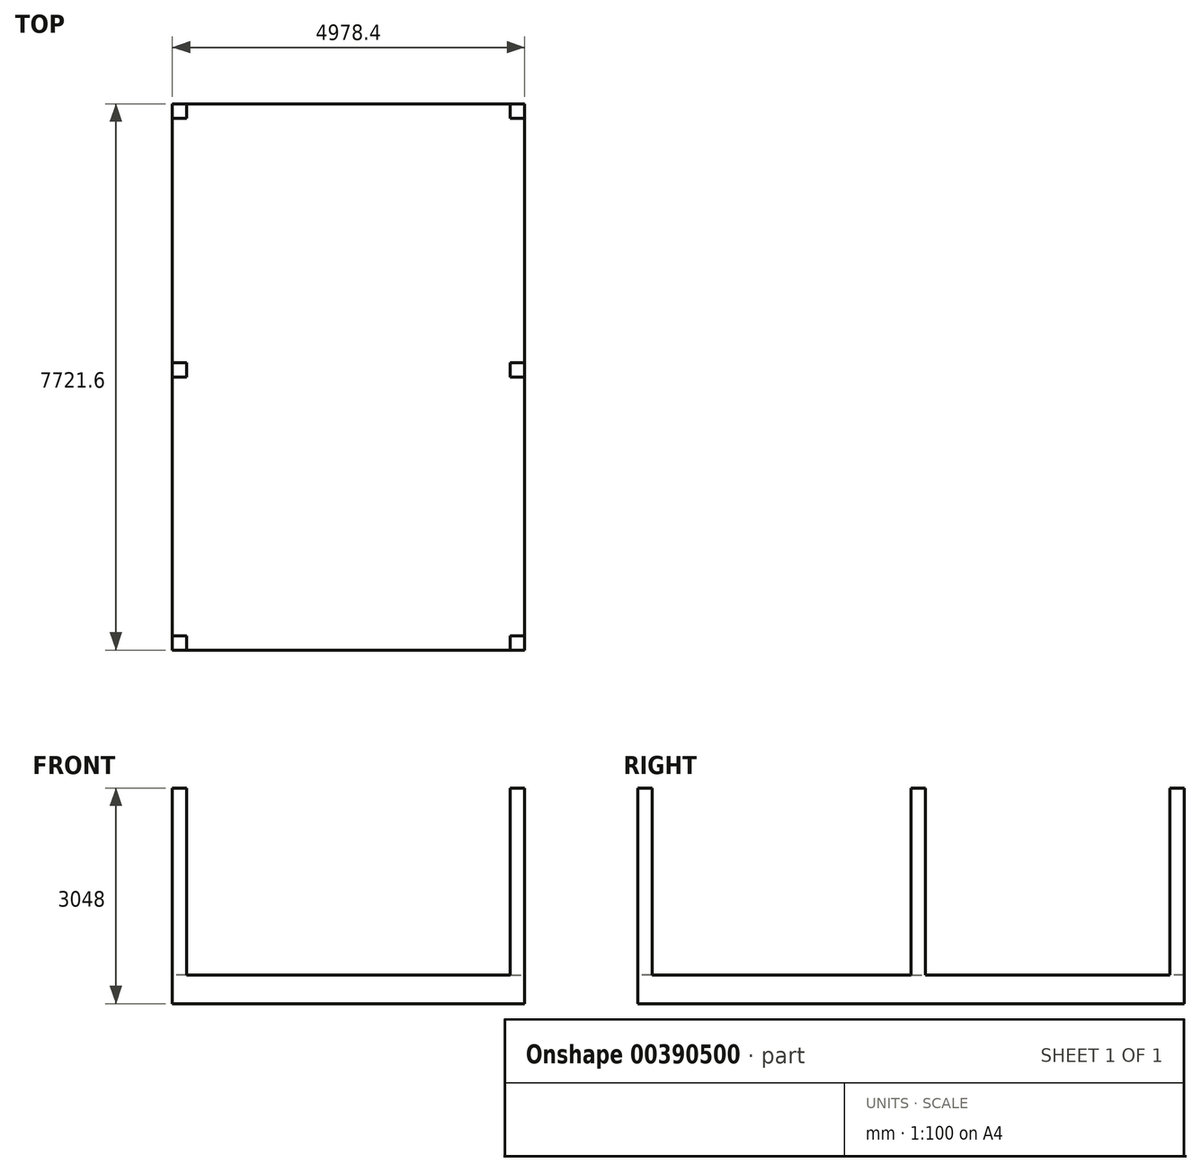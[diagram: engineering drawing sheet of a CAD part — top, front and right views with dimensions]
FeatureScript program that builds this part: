
annotation { "Feature Type Name" : "Feature", "Feature Type Description" : "" }
export const myFeature = defineFeature(function(context is Context, id is Id, definition is map)
    precondition{}
    {
        {
            var Q0;
            Q0=qCreatedBy(makeId("Top.planeOp"),FACE);
            var sketch = newSketch(context, id + "F0", { "sketchPlane" : qUnion([Q0])});
            skLineSegment(sketch, "E0.bottom", {"start": v(-2489.53, 5036.96) * mm, "end": v(2488.87, 5036.96) * mm});
            skLineSegment(sketch, "E0.top", {"start": v(-2489.53, -2684.64) * mm, "end": v(2488.87, -2684.64) * mm});
            skLineSegment(sketch, "E0.left", {"start": v(-2489.53, 5036.96) * mm, "end": v(-2489.53, -2684.64) * mm});
            skLineSegment(sketch, "E0.right", {"start": v(2488.87, 5036.96) * mm, "end": v(2488.87, -2684.64) * mm});
            skSolve(sketch);
        }
        {
            var Q0;
            Q0 = qSketchRegion(id + "F0", true);
            extrude(context, id + "F1", {"entities" : qUnion([Q0]), "oppositeDirection" : true, "depth" : 406.4 * mm});
        }
        {
            var Q0;
            Q0=makeQuery(id+"F1.opExtrude","SWEPT_FACE",FACE,{"disambiguationData":[OSD([sQuery(id+"F0.wireOp",EDGE,"E0.right")])]});
            var sketch = newSketch(context, id + "F2", { "sketchPlane" : qUnion([Q0])});
            skSolve(sketch);
        }
        {
            var Q0;
            Q0=makeQuery(id+"F1.opExtrude","CAP_FACE",FACE,{"disambiguationData":[OSD([sQuery(id+"F0.wireOp",EDGE,"E0.bottom"),sQuery(id+"F0.wireOp",EDGE,"E0.top"),sQuery(id+"F0.wireOp",EDGE,"E0.left"),sQuery(id+"F0.wireOp",EDGE,"E0.right")])],"isStart":false});
            var sketch = newSketch(context, id + "F3", { "sketchPlane" : qUnion([Q0])});
            skLineSegment(sketch, "E1.bottom", {"start": v(-2489.53, 2684.64) * mm, "end": v(-2286.33, 2684.64) * mm});
            skLineSegment(sketch, "E1.top", {"start": v(-2489.53, 2481.44) * mm, "end": v(-2286.33, 2481.44) * mm});
            skLineSegment(sketch, "E1.left", {"start": v(-2489.53, 2684.64) * mm, "end": v(-2489.53, 2481.44) * mm});
            skLineSegment(sketch, "E1.right", {"start": v(-2286.33, 2684.64) * mm, "end": v(-2286.33, 2481.44) * mm});
            skSolve(sketch);
        }
        {
            var Q0;
            Q0=makeQuery(id+"F3.imprint","IMPRINT",FACE,{"disambiguationData":[TD([[makeQuery(id+"F3.imprint","IMPRINT",EDGE,{"derivedFrom":sQuery(id+"F3.wireOp",EDGE,"E1.bottom")}),-1.0]])]});
            extrude(context, id + "F4", {"entities" : qUnion([Q0]), "operationType" : NewBodyOperationType.ADD, "oppositeDirection" : true, "depth" : 3048 * mm});
        }
        {
            var Q0;
            Q0=makeQuery(id+"F1.opExtrude","CAP_FACE",FACE,{"disambiguationData":[OSD([sQuery(id+"F0.wireOp",EDGE,"E0.bottom"),sQuery(id+"F0.wireOp",EDGE,"E0.top"),sQuery(id+"F0.wireOp",EDGE,"E0.left"),sQuery(id+"F0.wireOp",EDGE,"E0.right")])],"isStart":false});
            var sketch = newSketch(context, id + "F5", { "sketchPlane" : qUnion([Q0])});
            skLineSegment(sketch, "E2.bottom", {"start": v(2488.87, 2684.64) * mm, "end": v(2285.67, 2684.64) * mm});
            skLineSegment(sketch, "E2.top", {"start": v(2488.87, 2481.44) * mm, "end": v(2285.67, 2481.44) * mm});
            skLineSegment(sketch, "E2.left", {"start": v(2488.87, 2684.64) * mm, "end": v(2488.87, 2481.44) * mm});
            skLineSegment(sketch, "E2.right", {"start": v(2285.67, 2684.64) * mm, "end": v(2285.67, 2481.44) * mm});
            skSolve(sketch);
        }
        {
            var Q0;
            Q0=makeQuery(id+"F5.imprint","IMPRINT",FACE,{"disambiguationData":[TD([[makeQuery(id+"F5.imprint","IMPRINT",EDGE,{"derivedFrom":sQuery(id+"F5.wireOp",EDGE,"E2.bottom")}),-1.0]])]});
            extrude(context, id + "F6", {"entities" : qUnion([Q0]), "operationType" : NewBodyOperationType.ADD, "oppositeDirection" : true, "depth" : 3048 * mm});
        }
        {
            var Q0;
            Q0=makeQuery(id+"F0.imprint","IMPRINT",FACE,{"disambiguationData":[TD([[makeQuery(id+"F0.imprint","IMPRINT",EDGE,{"derivedFrom":sQuery(id+"F0.wireOp",EDGE,"E0.bottom")}),-1.0]])]});
            var sketch = newSketch(context, id + "F7", { "sketchPlane" : qUnion([Q0])});
            skSolve(sketch);
        }
        {
            var Q0;
            {var subQ2=sQuery(id+"F5.wireOp",EDGE,"E2.top");Q0=makeQuery(id+"F5.imprint","IMPRINT",FACE,{"disambiguationData":[TD([[makeQuery(id+"F5.imprint","IMPRINT",EDGE,{"derivedFrom":subQ2}),1.0]])]});}
            var sketch = newSketch(context, id + "F8", { "sketchPlane" : qUnion([Q0])});
            skLineSegment(sketch, "E3.bottom", {"start": v(2285.67, -4833.76) * mm, "end": v(2488.87, -4833.76) * mm});
            skLineSegment(sketch, "E3.top", {"start": v(2285.67, -5036.96) * mm, "end": v(2488.87, -5036.96) * mm});
            skLineSegment(sketch, "E3.left", {"start": v(2285.67, -4833.76) * mm, "end": v(2285.67, -5036.96) * mm});
            skLineSegment(sketch, "E3.right", {"start": v(2488.87, -4833.76) * mm, "end": v(2488.87, -5036.96) * mm});
            skSolve(sketch);
        }
        {
            var Q0;
            Q0 = qSketchRegion(id + "F8", true);
            extrude(context, id + "F9", {"entities" : qUnion([Q0]), "operationType" : NewBodyOperationType.ADD, "oppositeDirection" : true, "depth" : 3048 * mm});
        }
        {
            var Q0;
            {var subQ2=sQuery(id+"F5.wireOp",EDGE,"E2.top");Q0=makeQuery(id+"F5.imprint","IMPRINT",FACE,{"disambiguationData":[TD([[makeQuery(id+"F5.imprint","IMPRINT",EDGE,{"derivedFrom":subQ2}),1.0]])]});}
            var sketch = newSketch(context, id + "F10", { "sketchPlane" : qUnion([Q0])});
            skLineSegment(sketch, "E4.bottom", {"start": v(-2489.53, -4833.76) * mm, "end": v(-2286.33, -4833.76) * mm});
            skLineSegment(sketch, "E4.top", {"start": v(-2489.53, -5036.96) * mm, "end": v(-2286.33, -5036.96) * mm});
            skLineSegment(sketch, "E4.left", {"start": v(-2489.53, -4833.76) * mm, "end": v(-2489.53, -5036.96) * mm});
            skLineSegment(sketch, "E4.right", {"start": v(-2286.33, -4833.76) * mm, "end": v(-2286.33, -5036.96) * mm});
            skSolve(sketch);
        }
        {
            var Q0;
            Q0 = qSketchRegion(id + "F10", true);
            extrude(context, id + "F11", {"entities" : qUnion([Q0]), "operationType" : NewBodyOperationType.ADD, "oppositeDirection" : true, "depth" : 3048 * mm});
        }
        {
            var Q0;
            {var subQ2=sQuery(id+"F5.wireOp",EDGE,"E2.top");Q0=makeQuery(id+"F5.imprint","IMPRINT",FACE,{"disambiguationData":[TD([[makeQuery(id+"F5.imprint","IMPRINT",EDGE,{"derivedFrom":subQ2}),1.0]])]});}
            var sketch = newSketch(context, id + "F12", { "sketchPlane" : qUnion([Q0])});
            skLineSegment(sketch, "E5.bottom", {"start": v(-2286.33, -1379.36) * mm, "end": v(-2489.53, -1379.36) * mm});
            skLineSegment(sketch, "E5.top", {"start": v(-2286.33, -1176.16) * mm, "end": v(-2489.53, -1176.16) * mm});
            skLineSegment(sketch, "E5.left", {"start": v(-2286.33, -1379.36) * mm, "end": v(-2286.33, -1176.16) * mm});
            skLineSegment(sketch, "E5.right", {"start": v(-2489.53, -1379.36) * mm, "end": v(-2489.53, -1176.16) * mm});
            skSolve(sketch);
        }
        {
            var Q0;
            Q0 = qSketchRegion(id + "F12", true);
            extrude(context, id + "F13", {"entities" : qUnion([Q0]), "operationType" : NewBodyOperationType.ADD, "oppositeDirection" : true, "depth" : 3048 * mm});
        }
        {
            var Q0;
            {var subQ2=sQuery(id+"F5.wireOp",EDGE,"E2.top");Q0=makeQuery(id+"F5.imprint","IMPRINT",FACE,{"disambiguationData":[TD([[makeQuery(id+"F5.imprint","IMPRINT",EDGE,{"derivedFrom":subQ2}),1.0]])]});}
            var sketch = newSketch(context, id + "F14", { "sketchPlane" : qUnion([Q0])});
            skLineSegment(sketch, "E6.bottom", {"start": v(2488.87, -1379.36) * mm, "end": v(2285.67, -1379.36) * mm});
            skLineSegment(sketch, "E6.top", {"start": v(2488.87, -1176.16) * mm, "end": v(2285.67, -1176.16) * mm});
            skLineSegment(sketch, "E6.left", {"start": v(2488.87, -1379.36) * mm, "end": v(2488.87, -1176.16) * mm});
            skLineSegment(sketch, "E6.right", {"start": v(2285.67, -1379.36) * mm, "end": v(2285.67, -1176.16) * mm});
            skSolve(sketch);
        }
        {
            var Q0;
            Q0 = qSketchRegion(id + "F14", true);
            extrude(context, id + "F15", {"entities" : qUnion([Q0]), "operationType" : NewBodyOperationType.ADD, "oppositeDirection" : true, "depth" : 3048 * mm});
        }
        {
            var Q0;
            {var subQ0=sQuery(id+"F0.wireOp",EDGE,"E0.right");Q0=makeQuery(id+"F2.imprint","IMPRINT",FACE,{"disambiguationData":[TD([[makeQuery(id+"F2.imprint","IMPRINT",EDGE,{"derivedFrom":makeQuery(id+"F1.opExtrude","CAP_EDGE",EDGE,{"disambiguationData":[OSD([subQ0])],"isStart":true})}),1.0]])]});}
            var sketch = newSketch(context, id + "F16", { "sketchPlane" : qUnion([Q0])});
            skLineSegment(sketch, "E7", {"start": v(-2684.64, 0) * mm, "end": v(-2684.64, -158.75) * mm});
            skLineSegment(sketch, "E8", {"start": v(5036.96, 0) * mm, "end": v(5036.96, -406.4) * mm});
            skLineSegment(sketch, "E9", {"start": v(-2684.64, -158.75) * mm, "end": v(5036.96, -406.4) * mm});
            skLineSegment(sketch, "E10", {"start": v(-2684.64, 0) * mm, "end": v(5036.96, 0) * mm});
            skSolve(sketch);
        }
        {
            var Q0;
            Q0=makeQuery(id+"F7.imprint","IMPRINT",FACE,{"disambiguationData":[TD([[makeQuery(id+"F7.imprint","IMPRINT",EDGE,{"derivedFrom":makeQuery(id+"F0.imprint","IMPRINT",EDGE,{"derivedFrom":sQuery(id+"F0.wireOp",EDGE,"E0.bottom")})}),-1.0]])]});
            var sketch = newSketch(context, id + "F17", { "sketchPlane" : qUnion([Q0])});
            skLineSegment(sketch, "E11.bottom", {"start": v(2285.67, 4833.76) * mm, "end": v(2488.87, 4833.76) * mm});
            skLineSegment(sketch, "E11.top", {"start": v(2285.67, 1379.36) * mm, "end": v(2488.87, 1379.36) * mm});
            skLineSegment(sketch, "E11.left", {"start": v(2285.67, 4833.76) * mm, "end": v(2285.67, 1379.36) * mm});
            skLineSegment(sketch, "E11.right", {"start": v(2488.87, 4833.76) * mm, "end": v(2488.87, 1379.36) * mm});
            skSolve(sketch);
        }
        {
            var Q0;
            Q0 = qSketchRegion(id + "F17", true);
            extrude(context, id + "F18", {"entities" : qUnion([Q0]), "operationType" : NewBodyOperationType.ADD, "oppositeDirection" : true, "depth" : 203.2 * mm});
        }
    });
